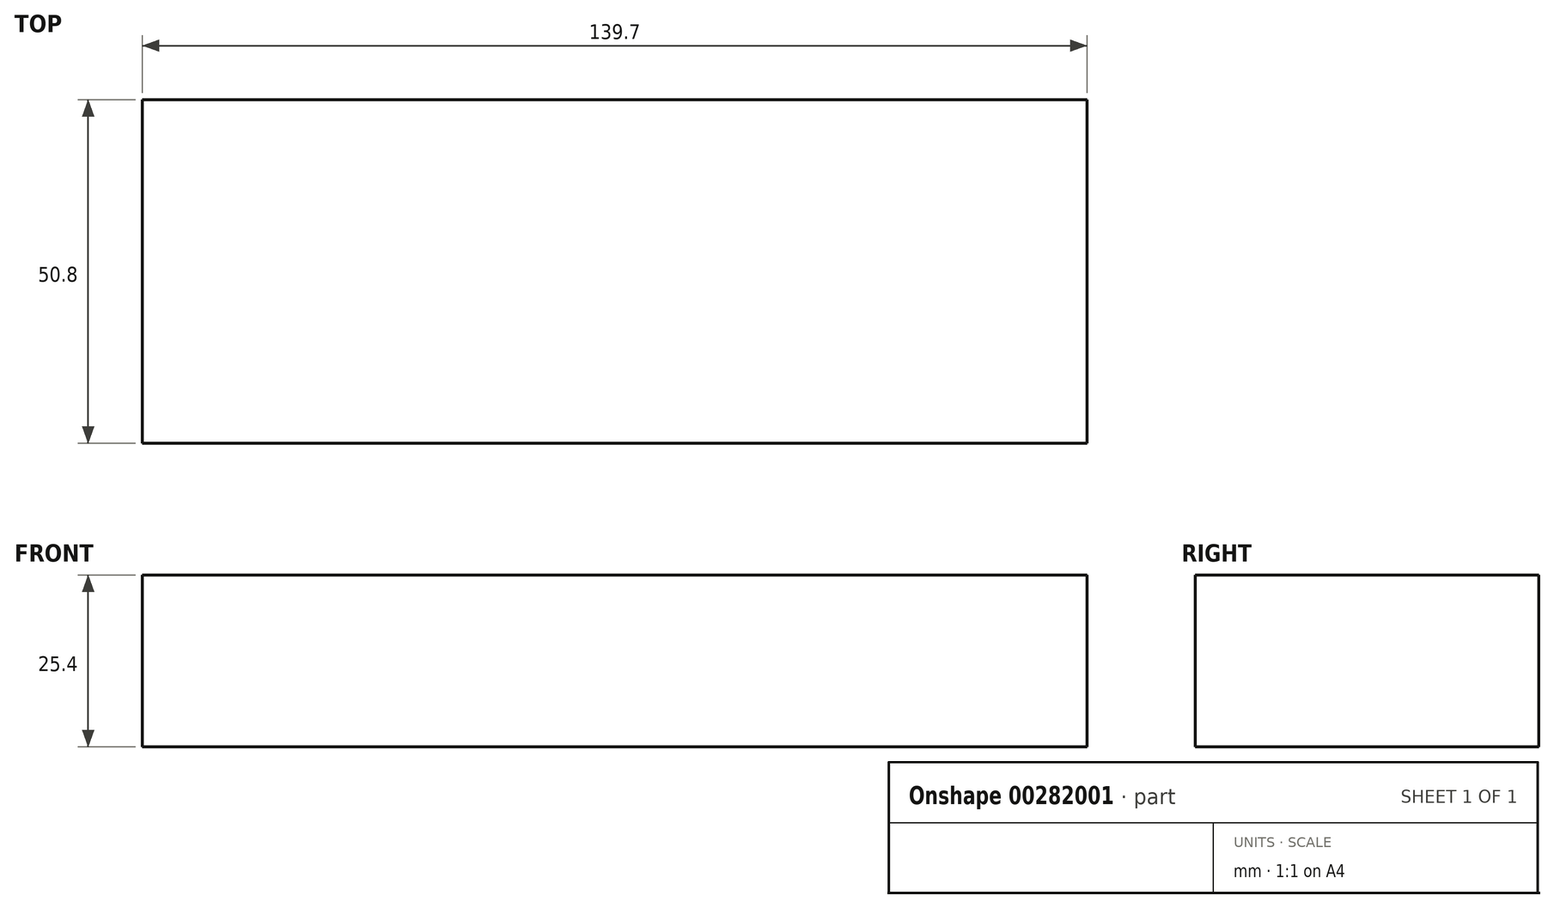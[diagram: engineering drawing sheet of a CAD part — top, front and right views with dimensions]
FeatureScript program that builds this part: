
annotation { "Feature Type Name" : "Feature", "Feature Type Description" : "" }
export const myFeature = defineFeature(function(context is Context, id is Id, definition is map)
    precondition{}
    {
        {
            var Q0;
            Q0=qCreatedBy(makeId("Top.planeOp"),FACE);
            var sketch = newSketch(context, id + "F0", { "sketchPlane" : qUnion([Q0])});
            skLineSegment(sketch, "E0.bottom", {"start": v(-58.14, 22.23) * mm, "end": v(81.56, 22.23) * mm});
            skLineSegment(sketch, "E0.top", {"start": v(-58.14, -28.57) * mm, "end": v(81.56, -28.57) * mm});
            skLineSegment(sketch, "E0.left", {"start": v(-58.14, 22.23) * mm, "end": v(-58.14, -28.57) * mm});
            skLineSegment(sketch, "E0.right", {"start": v(81.56, 22.23) * mm, "end": v(81.56, -28.57) * mm});
            skSolve(sketch);
        }
        {
            var Q0;
            Q0 = qSketchRegion(id + "F0", true);
            extrude(context, id + "F1", {"entities" : qUnion([Q0]), "depth" : 25.4 * mm});
        }
    });
